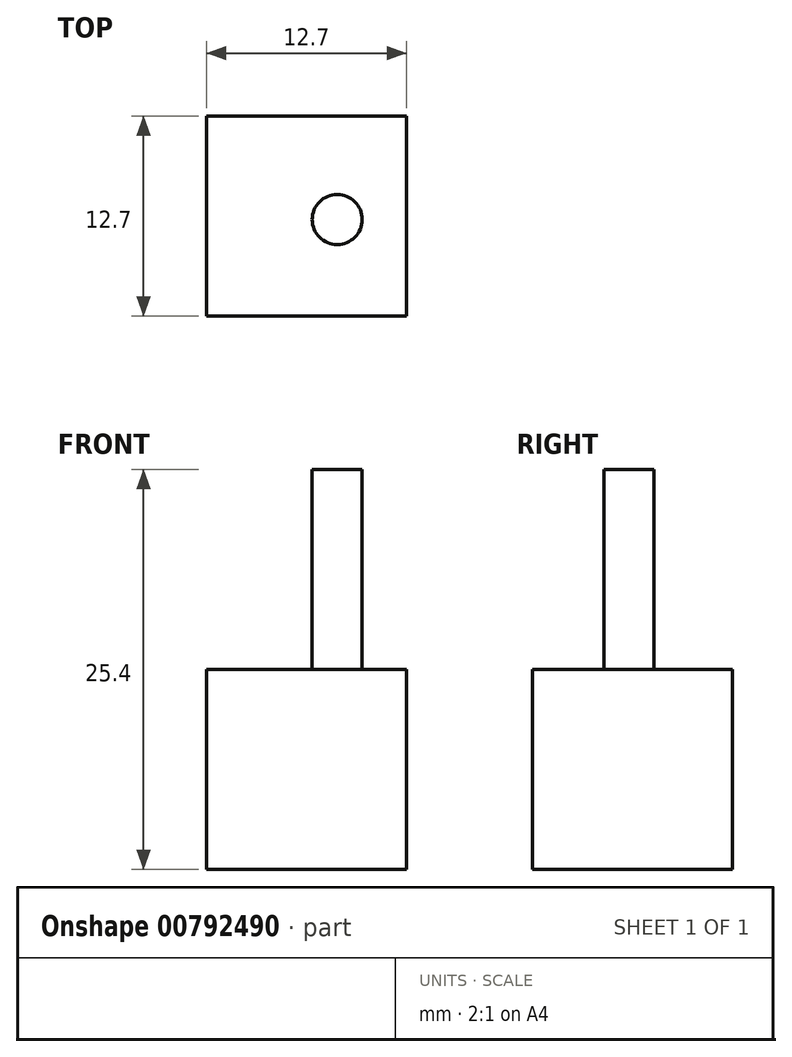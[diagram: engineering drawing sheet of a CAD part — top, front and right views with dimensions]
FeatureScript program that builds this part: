
annotation { "Feature Type Name" : "Feature", "Feature Type Description" : "" }
export const myFeature = defineFeature(function(context is Context, id is Id, definition is map)
    precondition{}
    {
        {
            var Q0;
            Q0=qCreatedBy(makeId("Front.planeOp"),FACE);
            var sketch = newSketch(context, id + "F0", { "sketchPlane" : qUnion([Q0])});
            skLineSegment(sketch, "E0.bottom", {"start": v(0, 0) * mm, "end": v(12.7, 0) * mm});
            skLineSegment(sketch, "E0.top", {"start": v(0, 12.7) * mm, "end": v(12.7, 12.7) * mm});
            skLineSegment(sketch, "E0.left", {"start": v(0, 0) * mm, "end": v(0, 12.7) * mm});
            skLineSegment(sketch, "E0.right", {"start": v(12.7, 0) * mm, "end": v(12.7, 12.7) * mm});
            skSolve(sketch);
        }
        {
            var Q0;
            Q0=qSketchRegion(id+"F0",true);
            extrude(context, id + "F1", {"entities" : qUnion([Q0]), "depth" : 12.7 * mm, "offsetDistance" : 25.4 * mm});
        }
        {
            var Q0;
            Q0=makeQuery(id+"F1.opExtrude","SWEPT_FACE",FACE,{"disambiguationData":[OSD([sQuery(id+"F0.wireOp",EDGE,"E0.top")])]});
            var sketch = newSketch(context, id + "F2", { "sketchPlane" : qUnion([Q0])});
            skCircle(sketch, "E1", {"center": v(8.3, -6.57) * mm, "radius": 1.59 * mm});
            skSolve(sketch);
        }
        {
            var Q0;
            Q0=qSketchRegion(id+"F2",true);
            extrude(context, id + "F3", {"entities" : qUnion([Q0]), "operationType" : NewBodyOperationType.ADD, "depth" : 12.7 * mm, "offsetDistance" : 25.4 * mm});
        }
    });
